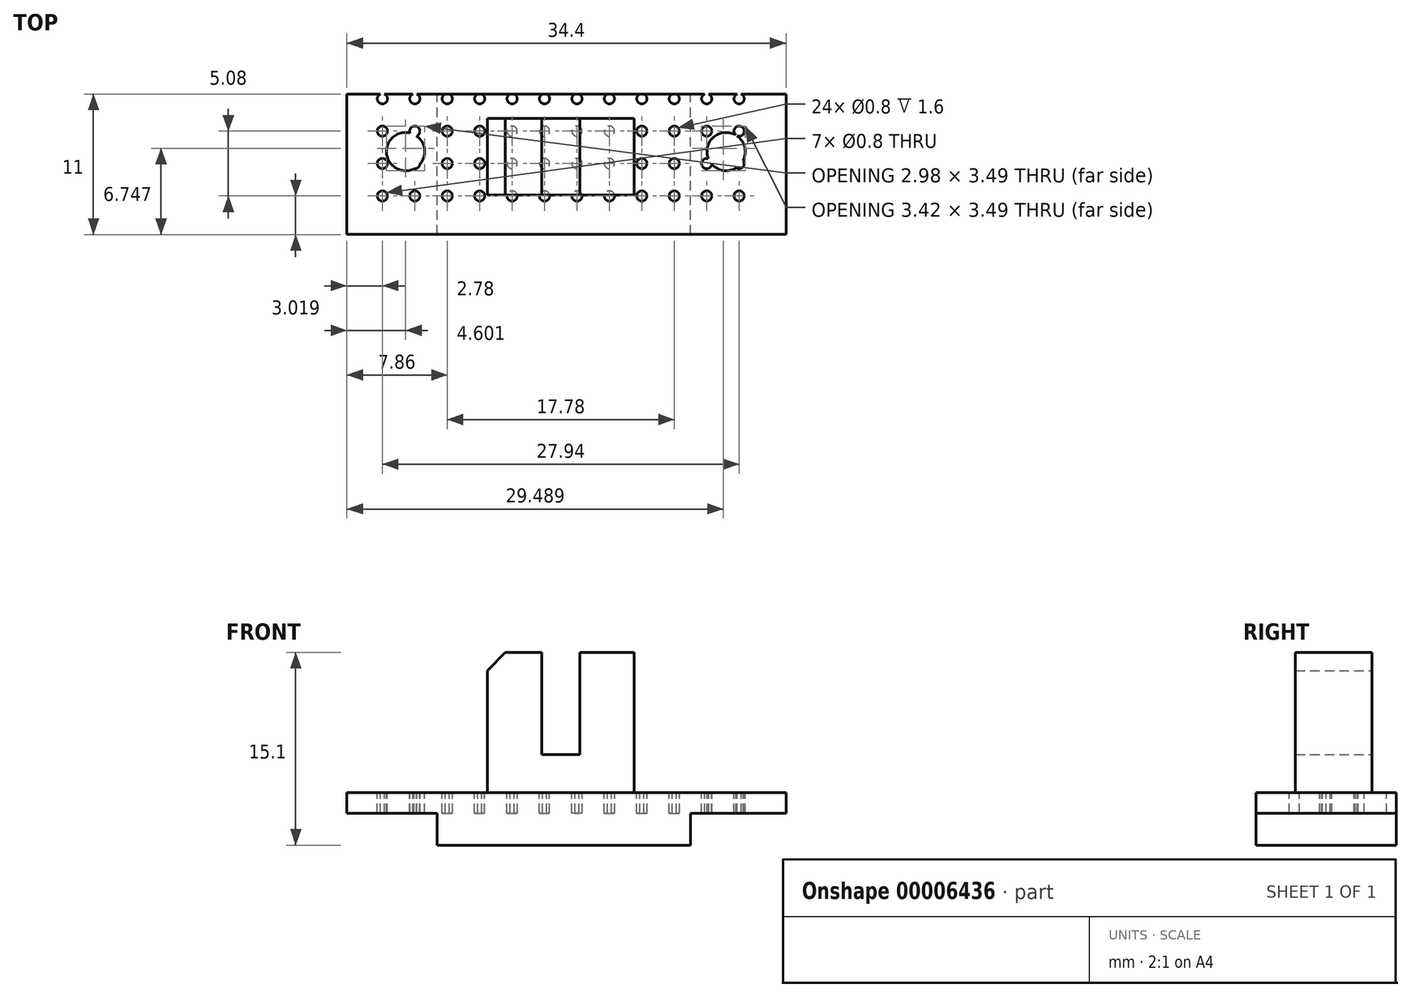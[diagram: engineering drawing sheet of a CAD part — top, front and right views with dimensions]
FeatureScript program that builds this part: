
annotation { "Feature Type Name" : "Feature", "Feature Type Description" : "" }
export const myFeature = defineFeature(function(context is Context, id is Id, definition is map)
    precondition{}
    {
        {
            var Q0;
            Q0=qCreatedBy(makeId("Front.planeOp"),FACE);
            var sketch = newSketch(context, id + "F0", { "sketchPlane" : qUnion([Q0])});
            skLineSegment(sketch, "E0", {"start": v(0, 0) * mm, "end": v(5.75, 0) * mm});
            skLineSegment(sketch, "E1", {"start": v(5.75, 0) * mm, "end": v(5.75, 11) * mm});
            skLineSegment(sketch, "E2", {"start": v(5.75, 11) * mm, "end": v(1.5, 11) * mm});
            skLineSegment(sketch, "E3", {"start": v(1.5, 11) * mm, "end": v(1.5, 3) * mm});
            skLineSegment(sketch, "E4", {"start": v(1.5, 3) * mm, "end": v(-1.5, 3) * mm});
            skLineSegment(sketch, "E5", {"start": v(-1.5, 3) * mm, "end": v(-1.5, 11) * mm});
            skLineSegment(sketch, "E6", {"start": v(-1.5, 11) * mm, "end": v(-4.34, 11) * mm});
            skLineSegment(sketch, "E7", {"start": v(-4.34, 11) * mm, "end": v(-5.75, 9.59) * mm});
            skLineSegment(sketch, "E8", {"start": v(-5.75, 9.59) * mm, "end": v(-5.75, 0) * mm});
            skLineSegment(sketch, "E9", {"start": v(-5.75, 0) * mm, "end": v(0, 0) * mm});
            skSolve(sketch);
        }
        {
            var Q0;
            Q0 = qSketchRegion(id + "F0", true);
            extrude(context, id + "F1", {"entities" : qUnion([Q0]), "depth" : 6 * mm});
        }
        {
            var Q0;
            Q0=qCreatedBy(makeId("Top.planeOp"),FACE);
            var sketch = newSketch(context, id + "F2", { "sketchPlane" : qUnion([Q0])});
            skLineSegment(sketch, "E10.bottom", {"start": v(-16.75, -9.1) * mm, "end": v(17.65, -9.1) * mm});
            skLineSegment(sketch, "E10.top", {"start": v(-16.75, 1.9) * mm, "end": v(17.65, 1.9) * mm});
            skLineSegment(sketch, "E10.left", {"start": v(-16.75, -9.1) * mm, "end": v(-16.75, 1.9) * mm});
            skLineSegment(sketch, "E10.right", {"start": v(17.65, -9.1) * mm, "end": v(17.65, 1.9) * mm});
            skCircle(sketch, "E11", {"center": v(-12.15, -2.6) * mm, "radius": 1.5 * mm});
            skCircle(sketch, "E12", {"center": v(12.95, -2.6) * mm, "radius": 1.5 * mm});
            skCircle(sketch, "E13", {"center": v(13.97, -6.08) * mm, "radius": 0.4 * mm});
            skCircle(sketch, "E14.1.0.0", {"center": v(11.43, -6.08) * mm, "radius": 0.4 * mm});
            skCircle(sketch, "E14.2.0.0", {"center": v(8.9, -6.08) * mm, "radius": 0.4 * mm});
            skCircle(sketch, "E14.3.0.0", {"center": v(6.35, -6.08) * mm, "radius": 0.4 * mm});
            skCircle(sketch, "E14.4.0.0", {"center": v(3.81, -6.08) * mm, "radius": 0.4 * mm});
            skCircle(sketch, "E14.5.0.0", {"center": v(1.27, -6.08) * mm, "radius": 0.4 * mm});
            skCircle(sketch, "E14.6.0.0", {"center": v(-1.27, -6.08) * mm, "radius": 0.4 * mm});
            skCircle(sketch, "E14.7.0.0", {"center": v(-3.8, -6.08) * mm, "radius": 0.4 * mm});
            skCircle(sketch, "E14.8.0.0", {"center": v(-6.35, -6.08) * mm, "radius": 0.4 * mm});
            skCircle(sketch, "E14.9.0.0", {"center": v(-8.89, -6.08) * mm, "radius": 0.4 * mm});
            skCircle(sketch, "E14.10.0.0", {"center": v(-11.43, -6.08) * mm, "radius": 0.4 * mm});
            skCircle(sketch, "E14.11.0.0", {"center": v(-13.97, -6.08) * mm, "radius": 0.4 * mm});
            skLineSegment(sketch, "E14.direction1", {"start": v(13.97, -6.08) * mm, "end": v(11.43, -6.08) * mm, "construction": true});
            skLineSegment(sketch, "E15.0.1.0", {"start": v(13.97, -3.54) * mm, "end": v(11.43, -3.54) * mm, "construction": true});
            skCircle(sketch, "E15.0.1.1", {"center": v(-13.97, -3.54) * mm, "radius": 0.4 * mm});
            skCircle(sketch, "E15.0.1.2", {"center": v(-11.43, -3.54) * mm, "radius": 0.4 * mm});
            skCircle(sketch, "E15.0.1.3", {"center": v(13.97, -3.54) * mm, "radius": 0.4 * mm});
            skCircle(sketch, "E15.0.1.4", {"center": v(-8.89, -3.54) * mm, "radius": 0.4 * mm});
            skCircle(sketch, "E15.0.1.5", {"center": v(-6.35, -3.54) * mm, "radius": 0.4 * mm});
            skCircle(sketch, "E15.0.1.6", {"center": v(-3.8, -3.54) * mm, "radius": 0.4 * mm});
            skCircle(sketch, "E15.0.1.7", {"center": v(11.43, -3.54) * mm, "radius": 0.4 * mm});
            skCircle(sketch, "E15.0.1.8", {"center": v(8.9, -3.54) * mm, "radius": 0.4 * mm});
            skCircle(sketch, "E15.0.1.9", {"center": v(6.35, -3.54) * mm, "radius": 0.4 * mm});
            skCircle(sketch, "E15.0.1.10", {"center": v(3.81, -3.54) * mm, "radius": 0.4 * mm});
            skCircle(sketch, "E15.0.1.11", {"center": v(1.27, -3.54) * mm, "radius": 0.4 * mm});
            skCircle(sketch, "E15.0.1.12", {"center": v(-1.27, -3.54) * mm, "radius": 0.4 * mm});
            skLineSegment(sketch, "E15.0.2.0", {"start": v(13.97, -1) * mm, "end": v(11.43, -1) * mm, "construction": true});
            skCircle(sketch, "E15.0.2.1", {"center": v(-13.97, -1) * mm, "radius": 0.4 * mm});
            skCircle(sketch, "E15.0.2.2", {"center": v(-11.43, -1) * mm, "radius": 0.4 * mm});
            skCircle(sketch, "E15.0.2.3", {"center": v(13.97, -1) * mm, "radius": 0.4 * mm});
            skCircle(sketch, "E15.0.2.4", {"center": v(-8.89, -1) * mm, "radius": 0.4 * mm});
            skCircle(sketch, "E15.0.2.5", {"center": v(-6.35, -1) * mm, "radius": 0.4 * mm});
            skCircle(sketch, "E15.0.2.6", {"center": v(-3.8, -1) * mm, "radius": 0.4 * mm});
            skCircle(sketch, "E15.0.2.7", {"center": v(11.43, -1) * mm, "radius": 0.4 * mm});
            skCircle(sketch, "E15.0.2.8", {"center": v(8.9, -1) * mm, "radius": 0.4 * mm});
            skCircle(sketch, "E15.0.2.9", {"center": v(6.35, -1) * mm, "radius": 0.4 * mm});
            skCircle(sketch, "E15.0.2.10", {"center": v(3.81, -1) * mm, "radius": 0.4 * mm});
            skCircle(sketch, "E15.0.2.11", {"center": v(1.27, -1) * mm, "radius": 0.4 * mm});
            skCircle(sketch, "E15.0.2.12", {"center": v(-1.27, -1) * mm, "radius": 0.4 * mm});
            skLineSegment(sketch, "E15.0.3.0", {"start": v(13.97, 1.54) * mm, "end": v(11.43, 1.54) * mm, "construction": true});
            skCircle(sketch, "E15.0.3.1", {"center": v(-13.97, 1.54) * mm, "radius": 0.4 * mm});
            skCircle(sketch, "E15.0.3.2", {"center": v(-11.43, 1.54) * mm, "radius": 0.4 * mm});
            skCircle(sketch, "E15.0.3.3", {"center": v(13.97, 1.54) * mm, "radius": 0.4 * mm});
            skCircle(sketch, "E15.0.3.4", {"center": v(-8.89, 1.54) * mm, "radius": 0.4 * mm});
            skCircle(sketch, "E15.0.3.5", {"center": v(-6.35, 1.54) * mm, "radius": 0.4 * mm});
            skCircle(sketch, "E15.0.3.6", {"center": v(-3.8, 1.54) * mm, "radius": 0.4 * mm});
            skCircle(sketch, "E15.0.3.7", {"center": v(11.43, 1.54) * mm, "radius": 0.4 * mm});
            skCircle(sketch, "E15.0.3.8", {"center": v(8.9, 1.54) * mm, "radius": 0.4 * mm});
            skCircle(sketch, "E15.0.3.9", {"center": v(6.35, 1.54) * mm, "radius": 0.4 * mm});
            skCircle(sketch, "E15.0.3.10", {"center": v(3.81, 1.54) * mm, "radius": 0.4 * mm});
            skCircle(sketch, "E15.0.3.11", {"center": v(1.27, 1.54) * mm, "radius": 0.4 * mm});
            skCircle(sketch, "E15.0.3.12", {"center": v(-1.27, 1.54) * mm, "radius": 0.4 * mm});
            skLineSegment(sketch, "E15.0.4.0", {"start": v(13.97, 4.08) * mm, "end": v(11.43, 4.08) * mm, "construction": true});
            skCircle(sketch, "E15.0.4.1", {"center": v(-13.97, 4.08) * mm, "radius": 0.4 * mm});
            skCircle(sketch, "E15.0.4.2", {"center": v(-11.43, 4.08) * mm, "radius": 0.4 * mm});
            skCircle(sketch, "E15.0.4.3", {"center": v(13.97, 4.08) * mm, "radius": 0.4 * mm});
            skCircle(sketch, "E15.0.4.4", {"center": v(-8.89, 4.08) * mm, "radius": 0.4 * mm});
            skCircle(sketch, "E15.0.4.5", {"center": v(-6.35, 4.08) * mm, "radius": 0.4 * mm});
            skCircle(sketch, "E15.0.4.6", {"center": v(-3.8, 4.08) * mm, "radius": 0.4 * mm});
            skCircle(sketch, "E15.0.4.7", {"center": v(11.43, 4.08) * mm, "radius": 0.4 * mm});
            skCircle(sketch, "E15.0.4.8", {"center": v(8.9, 4.08) * mm, "radius": 0.4 * mm});
            skCircle(sketch, "E15.0.4.9", {"center": v(6.35, 4.08) * mm, "radius": 0.4 * mm});
            skCircle(sketch, "E15.0.4.10", {"center": v(3.81, 4.08) * mm, "radius": 0.4 * mm});
            skCircle(sketch, "E15.0.4.11", {"center": v(1.27, 4.08) * mm, "radius": 0.4 * mm});
            skCircle(sketch, "E15.0.4.12", {"center": v(-1.27, 4.08) * mm, "radius": 0.4 * mm});
            skLineSegment(sketch, "E15.direction1", {"start": v(11.43, -6.08) * mm, "end": v(26.8, -6.08) * mm, "construction": true});
            skLineSegment(sketch, "E15.direction2", {"start": v(11.43, -6.08) * mm, "end": v(11.43, -3.54) * mm, "construction": true});
            skSolve(sketch);
        }
        {
            var Q0;
            Q0=makeQuery(id+"F2.imprint","IMPRINT",FACE,{"disambiguationData":[TD([[makeQuery(id+"F2.imprint","IMPRINT",EDGE,{"derivedFrom":sQuery(id+"F2.wireOp",EDGE,"E10.bottom")}),1.0]])]});
            extrude(context, id + "F3", {"entities" : qUnion([Q0]), "operationType" : NewBodyOperationType.ADD, "oppositeDirection" : true, "depth" : 1.6 * mm});
        }
        {
            var Q0;
            Q0=makeQuery(id+"F3.opExtrude","CAP_FACE",FACE,{"disambiguationData":[OSD([sQuery(id+"F2.wireOp",EDGE,"E10.bottom"),sQuery(id+"F2.wireOp",EDGE,"E10.top"),sQuery(id+"F2.wireOp",EDGE,"E10.left"),sQuery(id+"F2.wireOp",EDGE,"E10.right"),sQuery(id+"F2.wireOp",EDGE,"E11"),sQuery(id+"F2.wireOp",EDGE,"E12"),sQuery(id+"F2.wireOp",EDGE,"E13"),sQuery(id+"F2.wireOp",EDGE,"E14.1.0.0"),sQuery(id+"F2.wireOp",EDGE,"E14.2.0.0"),sQuery(id+"F2.wireOp",EDGE,"E14.3.0.0"),sQuery(id+"F2.wireOp",EDGE,"E14.4.0.0"),sQuery(id+"F2.wireOp",EDGE,"E14.5.0.0"),sQuery(id+"F2.wireOp",EDGE,"E14.6.0.0"),sQuery(id+"F2.wireOp",EDGE,"E14.7.0.0"),sQuery(id+"F2.wireOp",EDGE,"E14.8.0.0"),sQuery(id+"F2.wireOp",EDGE,"E14.9.0.0"),sQuery(id+"F2.wireOp",EDGE,"E14.10.0.0"),sQuery(id+"F2.wireOp",EDGE,"E14.11.0.0"),sQuery(id+"F2.wireOp",EDGE,"E15.0.1.1"),sQuery(id+"F2.wireOp",EDGE,"E15.0.1.2"),sQuery(id+"F2.wireOp",EDGE,"E15.0.1.3"),sQuery(id+"F2.wireOp",EDGE,"E15.0.1.4"),sQuery(id+"F2.wireOp",EDGE,"E15.0.1.5"),sQuery(id+"F2.wireOp",EDGE,"E15.0.1.6"),sQuery(id+"F2.wireOp",EDGE,"E15.0.1.7"),sQuery(id+"F2.wireOp",EDGE,"E15.0.1.8"),sQuery(id+"F2.wireOp",EDGE,"E15.0.1.9"),sQuery(id+"F2.wireOp",EDGE,"E15.0.1.10"),sQuery(id+"F2.wireOp",EDGE,"E15.0.1.11"),sQuery(id+"F2.wireOp",EDGE,"E15.0.1.12"),sQuery(id+"F2.wireOp",EDGE,"E15.0.2.1"),sQuery(id+"F2.wireOp",EDGE,"E15.0.2.2"),sQuery(id+"F2.wireOp",EDGE,"E15.0.2.3"),sQuery(id+"F2.wireOp",EDGE,"E15.0.2.4"),sQuery(id+"F2.wireOp",EDGE,"E15.0.2.5"),sQuery(id+"F2.wireOp",EDGE,"E15.0.2.6"),sQuery(id+"F2.wireOp",EDGE,"E15.0.2.7"),sQuery(id+"F2.wireOp",EDGE,"E15.0.2.8"),sQuery(id+"F2.wireOp",EDGE,"E15.0.2.9"),sQuery(id+"F2.wireOp",EDGE,"E15.0.2.10"),sQuery(id+"F2.wireOp",EDGE,"E15.0.2.11"),sQuery(id+"F2.wireOp",EDGE,"E15.0.2.12"),sQuery(id+"F2.wireOp",EDGE,"E15.0.3.1"),sQuery(id+"F2.wireOp",EDGE,"E15.0.3.2"),sQuery(id+"F2.wireOp",EDGE,"E15.0.3.3"),sQuery(id+"F2.wireOp",EDGE,"E15.0.3.4"),sQuery(id+"F2.wireOp",EDGE,"E15.0.3.5"),sQuery(id+"F2.wireOp",EDGE,"E15.0.3.6"),sQuery(id+"F2.wireOp",EDGE,"E15.0.3.7"),sQuery(id+"F2.wireOp",EDGE,"E15.0.3.8"),sQuery(id+"F2.wireOp",EDGE,"E15.0.3.9"),sQuery(id+"F2.wireOp",EDGE,"E15.0.3.10"),sQuery(id+"F2.wireOp",EDGE,"E15.0.3.11"),sQuery(id+"F2.wireOp",EDGE,"E15.0.3.12")])],"isStart":false});
            var sketch = newSketch(context, id + "F4", { "sketchPlane" : qUnion([Q0])});
            skLineSegment(sketch, "E16.bottom", {"start": v(-9.68, 9.1) * mm, "end": v(10.16, 9.1) * mm});
            skLineSegment(sketch, "E16.top", {"start": v(-9.68, -1.9) * mm, "end": v(10.16, -1.9) * mm});
            skLineSegment(sketch, "E16.left", {"start": v(-9.68, 9.1) * mm, "end": v(-9.68, -1.9) * mm});
            skLineSegment(sketch, "E16.right", {"start": v(10.16, 9.1) * mm, "end": v(10.16, -1.9) * mm});
            skSolve(sketch);
        }
        {
            var Q0;
            Q0 = qSketchRegion(id + "F4", true);
            extrude(context, id + "F5", {"entities" : qUnion([Q0]), "operationType" : NewBodyOperationType.ADD, "depth" : 2.5 * mm});
        }
    });
